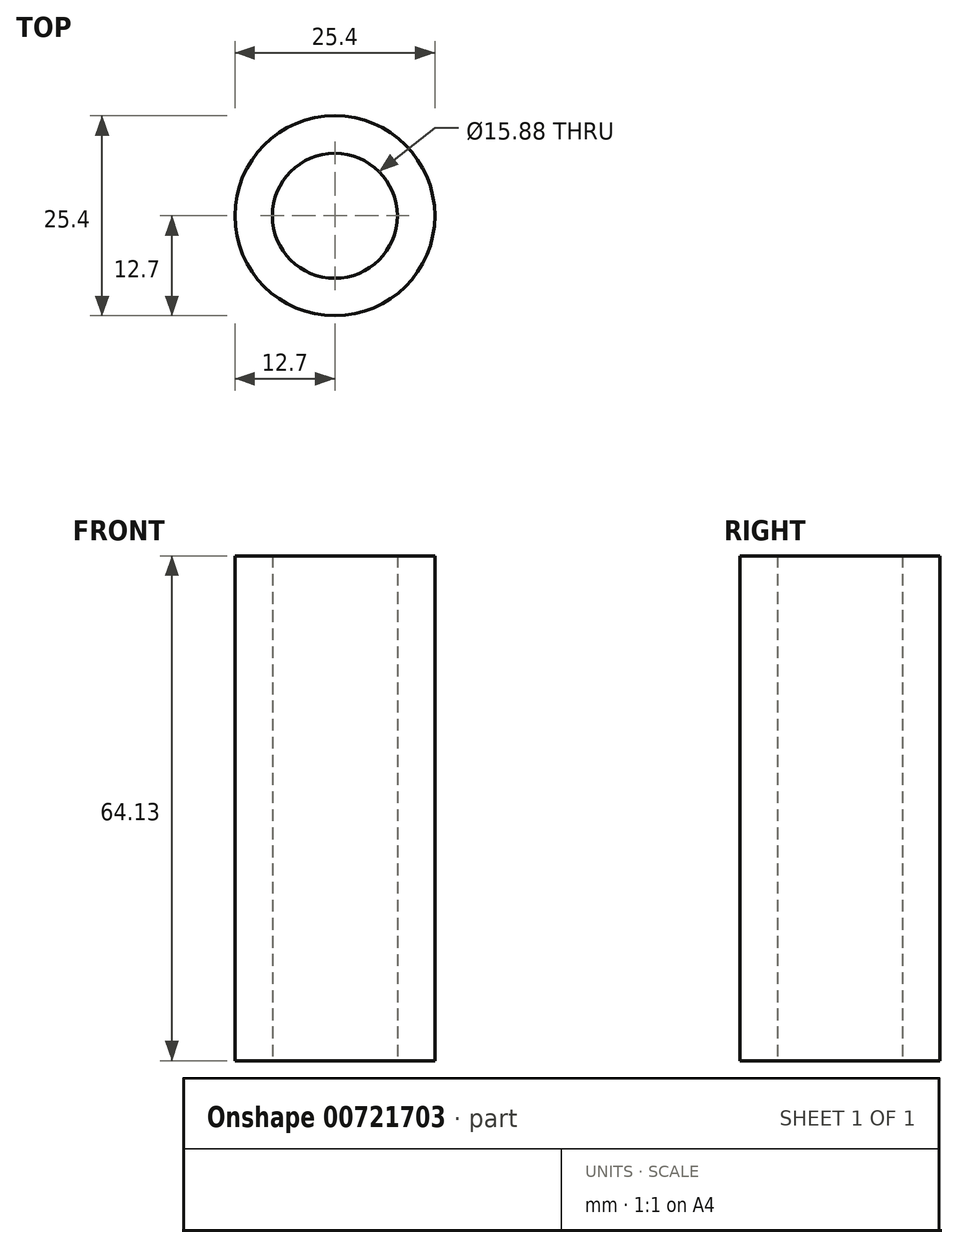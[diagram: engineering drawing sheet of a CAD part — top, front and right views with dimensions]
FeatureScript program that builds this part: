
annotation { "Feature Type Name" : "Feature", "Feature Type Description" : "" }
export const myFeature = defineFeature(function(context is Context, id is Id, definition is map)
    precondition{}
    {
        {
            var Q0;
            Q0=qCreatedBy(makeId("Front.planeOp"),FACE);
            var sketch = newSketch(context, id + "F0", { "sketchPlane" : qUnion([Q0])});
            skPoint(sketch, "E0.visualSharp", {"position": v(4518.56, 0) * mm});
            skPoint(sketch, "E1.orphan", {"position": v(-4518.56, 0) * mm});
            skLineSegment(sketch, "E2.MirrorCS", {"start": v(0, 64.13) * mm, "end": v(0, 0) * mm});
            skSolve(sketch);
        }
        {
            var Q0;
            Q0=sQuery(id+"F0.wireOp",VERTEX,"E2.MirrorCS.start");
            var Q1;
            Q1=qCreatedBy(makeId("Top.planeOp"),FACE);
            cPlane(context, id + "F1", {"entities" : qUnion([Q0, Q1]), "cplaneType" : CPlaneType.PLANE_POINT, "offset" : 381 * mm, "width" : 152.4 * mm, "height" : 152.4 * mm});
        }
        {
            var Q0;
            Q0=qCreatedBy(id+"F1.planeOp",FACE);
            var sketch = newSketch(context, id + "F2", { "sketchPlane" : qUnion([Q0])});
            skCircle(sketch, "E3", {"center": v(0, 0) * mm, "radius": 12.7 * mm});
            skCircle(sketch, "E4", {"center": v(0, 0) * mm, "radius": 7.94 * mm});
            skSolve(sketch);
        }
        {
            var Q0;
            Q0=qSketchRegion(id+"F2",true);
            var Q1;
            Q1=qConstructionFilter(qBodyType(qCreatedBy(id+"F0",EDGE),BodyType.WIRE),ConstructionObject.NO);
            sweep(context, id + "F3", {"profiles" : qUnion([Q0]), "path" : qUnion([Q1])});
        }
    });
